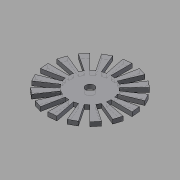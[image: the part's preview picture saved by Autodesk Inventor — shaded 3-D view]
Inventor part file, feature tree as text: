
AUTODESK INVENTOR PART (.ipt)
format: ipt  version: 2015 (Build 190159000, 159)  size: 174,592 bytes
history: native  units: in
note: dims shown in document units (in); Inventor stores cm internally (conversion verified against a paired STEP export)
features: other x3, sketch x1
ambient origin geometry x8: Origin, YZ Plane, XZ Plane, XY Plane, X Axis, Y Axis, Z Axis, Center Point
bodies: Solid1 (feature_tree)
feature tree (4):
  other  "encoder_MIR3.ipt"
  other  "Solid1::encoder_MIR3.ipt"
  other  "TaggingFeature1"
  sketch  "Sketch1"  dims[d0=0.3937in]
